# Revit family: Power-ModularDevices-GEWISS-90AM-SPD_TYPE1+2_1PN_25kA
name_source: partatom
category: Apparecchi elettrici
revit_build: Autodesk Revit 2016 (Build: 20161004_0715(x64)
units: mm (PartAtom-declared; Revit-internal decimal feet)

## family parameters
Condiviso = No
Host = Superficie
Mantenere orientamento annotazione = Sì
Numero OmniClass = 23.80.50.00
Punto di calcolo locali = Sì
Quota connettore circolare = Usa diametro
Taglio con vuoti quando caricato = No
Tipo di parte = Normale
Titolo OmniClass = Terminals for Power Supply

## types (1)
- GWD6404 - LST - SPD 1P+N 25KA AUX. T1+2
    Catalogue = POWER
    Catalogue Range = 90 AM
    Descrizione = LST - SPD 1P+N 25KA AUX. T1+2
    EAN code = 8011564774827
    Electrocod = 0641
    IDF = c10255b5-4ec2-446d-ba9d-d686e9f5ba9b
    IDT = 4e618f7d-67d6-4cf4-8899-ed9f15f30b0f
    Immagine tipo = GWD6404.jpg
    Impulse current: = 25KA
    Maximum discharge current: = 100KA
    Modello = GWD6404
    No. Chorus modules = 4
    No. of modules EN 50022 = 4
    No. of poles = 1P+N
    Number of poles = 1P+N
    Numero di poli_ = 1
    Produttore = GEWISS S.p.A.
    Prospetto di default = 1219 mm
    Rated voltage = 230Vac
    Rated voltage AC = 230V
    SEO = Limiter
    Simbolo in pianta = Sì
    Spostamento_x = -3950 mm  [stored -12.9593 ft]
    Technical sheet = https://www.gewiss.com
    Type = 1+2
    Type: = 1+2
    URL = https://www.gewiss.com
    Version file RFA = 18.0
    carico = Altro
    potenza in watt = 0 V

note: [stored X ft] marks values corroborated as IEEE doubles in the binary element streams (Revit-internal decimal feet)
